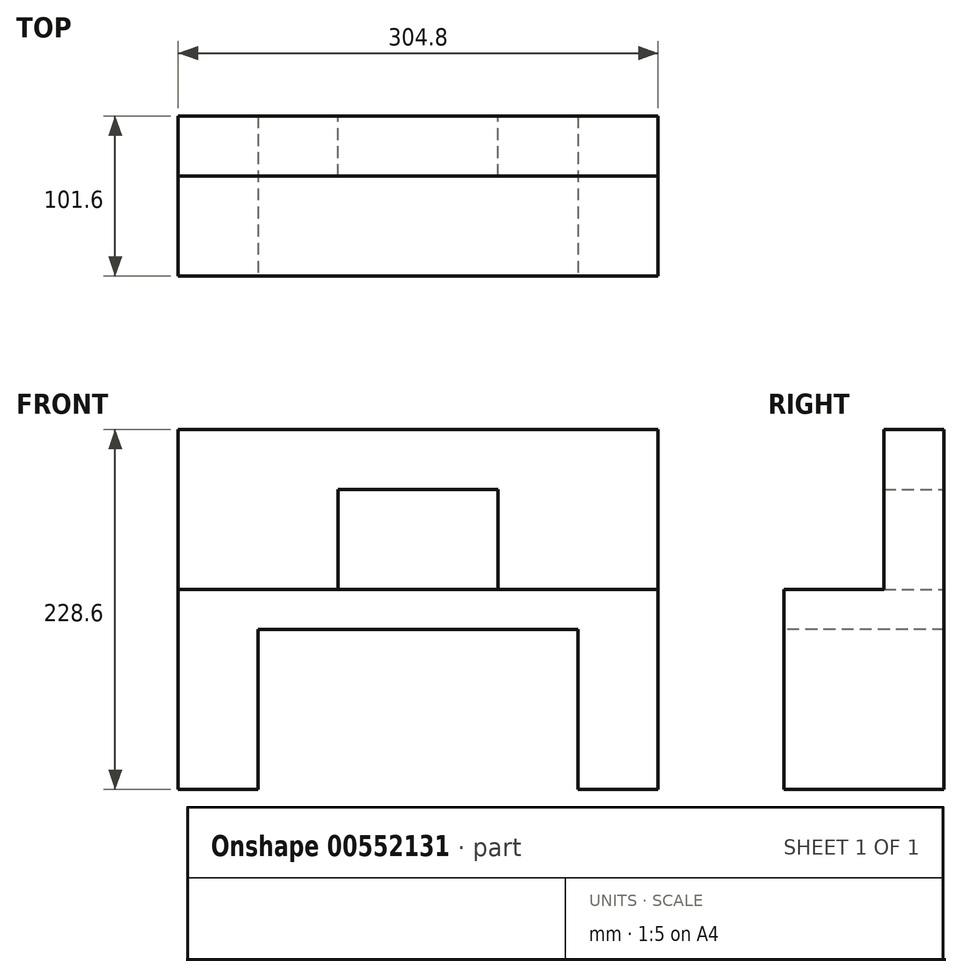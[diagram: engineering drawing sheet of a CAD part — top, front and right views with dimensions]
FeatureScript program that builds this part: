
annotation { "Feature Type Name" : "Feature", "Feature Type Description" : "" }
export const myFeature = defineFeature(function(context is Context, id is Id, definition is map)
    precondition{}
    {
        {
            var Q0;
            Q0=qCreatedBy(makeId("Top.planeOp"),FACE);
            var sketch = newSketch(context, id + "F0", { "sketchPlane" : qUnion([Q0])});
            skLineSegment(sketch, "E0.bottom", {"start": v(-249.47, 52.33) * mm, "end": v(55.33, 52.33) * mm});
            skLineSegment(sketch, "E0.top", {"start": v(-249.47, -49.27) * mm, "end": v(55.33, -49.27) * mm});
            skLineSegment(sketch, "E0.left", {"start": v(-249.47, 52.33) * mm, "end": v(-249.47, -49.27) * mm});
            skLineSegment(sketch, "E0.right", {"start": v(55.33, 52.33) * mm, "end": v(55.33, -49.27) * mm});
            skSolve(sketch);
        }
        {
            var Q0;
            Q0=makeQuery(id+"F0.imprint","IMPRINT",FACE,{"disambiguationData":[TD([[makeQuery(id+"F0.imprint","IMPRINT",EDGE,{"derivedFrom":sQuery(id+"F0.wireOp",EDGE,"E0.bottom")}),-1.0]])]});
            extrude(context, id + "F1", {"entities" : qUnion([Q0]), "depth" : 127 * mm, "offsetDistance" : 25.4 * mm});
        }
        {
            var Q0;
            Q0=makeQuery(id+"F1.opExtrude","SWEPT_FACE",FACE,{"disambiguationData":[OSD([sQuery(id+"F0.wireOp",EDGE,"E0.top")])]});
            var sketch = newSketch(context, id + "F2", { "sketchPlane" : qUnion([Q0])});
            skLineSegment(sketch, "E1", {"start": v(-198.67, 0) * mm, "end": v(-198.67, 127) * mm});
            skLineSegment(sketch, "E2", {"start": v(4.53, 0) * mm, "end": v(4.53, 127) * mm});
            skLineSegment(sketch, "E3", {"start": v(-198.67, 101.6) * mm, "end": v(4.53, 101.6) * mm});
            skLineSegment(sketch, "E4.bottom", {"start": v(-249.47, 127) * mm, "end": v(-198.67, 127) * mm});
            skLineSegment(sketch, "E4.top", {"start": v(-249.47, 63.5) * mm, "end": v(-198.67, 63.5) * mm});
            skLineSegment(sketch, "E4.left", {"start": v(-249.47, 127) * mm, "end": v(-249.47, 63.5) * mm});
            skLineSegment(sketch, "E4.right", {"start": v(-198.67, 127) * mm, "end": v(-198.67, 63.5) * mm});
            skLineSegment(sketch, "E5.bottom", {"start": v(4.53, 127) * mm, "end": v(55.33, 127) * mm});
            skLineSegment(sketch, "E5.top", {"start": v(4.53, 63.5) * mm, "end": v(55.33, 63.5) * mm});
            skLineSegment(sketch, "E5.left", {"start": v(4.53, 127) * mm, "end": v(4.53, 63.5) * mm});
            skLineSegment(sketch, "E5.right", {"start": v(55.33, 127) * mm, "end": v(55.33, 63.5) * mm});
            skLineSegment(sketch, "E6.top", {"start": v(-249.47, 0) * mm, "end": v(-198.67, 0) * mm});
            skLineSegment(sketch, "E6.left", {"start": v(-249.47, 63.5) * mm, "end": v(-249.47, 0) * mm});
            skLineSegment(sketch, "E6.right", {"start": v(-198.67, 63.5) * mm, "end": v(-198.67, 0) * mm});
            skLineSegment(sketch, "E7.top", {"start": v(4.53, 0) * mm, "end": v(55.33, 0) * mm});
            skLineSegment(sketch, "E7.left", {"start": v(4.53, 63.5) * mm, "end": v(4.53, 0) * mm});
            skLineSegment(sketch, "E7.right", {"start": v(55.33, 63.5) * mm, "end": v(55.33, 0) * mm});
            skLineSegment(sketch, "E8.bottom", {"start": v(-198.67, 127) * mm, "end": v(4.53, 127) * mm});
            skLineSegment(sketch, "E8.left", {"start": v(-198.67, 127) * mm, "end": v(-198.67, 101.6) * mm});
            skLineSegment(sketch, "E8.right", {"start": v(4.53, 127) * mm, "end": v(4.53, 101.6) * mm});
            skLineSegment(sketch, "E9.top", {"start": v(-198.67, 0) * mm, "end": v(4.53, 0) * mm});
            skLineSegment(sketch, "E9.left", {"start": v(-198.67, 101.6) * mm, "end": v(-198.67, 0) * mm});
            skLineSegment(sketch, "E9.right", {"start": v(4.53, 101.6) * mm, "end": v(4.53, 0) * mm});
            skSolve(sketch);
        }
        {
            var Q0;
            {var subQ3=sQuery(id+"F2.wireOp",EDGE,"E3");Q0=makeQuery(id+"F2.imprint","IMPRINT",FACE,{"disambiguationData":[TD([[makeQuery(id+"F2.imprint","IMPRINT",EDGE,{"derivedFrom":subQ3}),-1.0]])]});}
            extrude(context, id + "F3", {"entities" : qUnion([Q0]), "operationType" : NewBodyOperationType.REMOVE, "endBound" : BoundingType.THROUGH_ALL, "oppositeDirection" : true, "depth" : 25.4 * mm, "offsetDistance" : 25.4 * mm});
        }
        {
            var Q0;
            Q0=makeQuery(id+"F1.opExtrude","CAP_FACE",FACE,{"disambiguationData":[OSD([sQuery(id+"F0.wireOp",EDGE,"E0.bottom"),sQuery(id+"F0.wireOp",EDGE,"E0.top"),sQuery(id+"F0.wireOp",EDGE,"E0.left"),sQuery(id+"F0.wireOp",EDGE,"E0.right")])],"isStart":false});
            var sketch = newSketch(context, id + "F4", { "sketchPlane" : qUnion([Q0])});
            skLineSegment(sketch, "E10", {"start": v(-249.47, 14.23) * mm, "end": v(55.33, 14.23) * mm});
            skLineSegment(sketch, "E11", {"start": v(-198.67, 14.23) * mm, "end": v(-198.67, 52.33) * mm});
            skLineSegment(sketch, "E12", {"start": v(4.53, 14.23) * mm, "end": v(4.53, 52.33) * mm});
            skLineSegment(sketch, "E13", {"start": v(-147.87, 14.23) * mm, "end": v(-147.87, 52.33) * mm});
            skLineSegment(sketch, "E14", {"start": v(-46.27, 14.23) * mm, "end": v(-46.27, 52.33) * mm});
            skSolve(sketch);
        }
        {
            var Q0;
            {var subQ3=sQuery(id+"F4.wireOp",EDGE,"E11");Q0=makeQuery(id+"F4.imprint","IMPRINT",FACE,{"disambiguationData":[TD([[makeQuery(id+"F4.imprint","IMPRINT",EDGE,{"derivedFrom":subQ3}),1.0]])]});}
            var Q1;
            {var subQ0=sQuery(id+"F4.wireOp",EDGE,"E11");Q1=makeQuery(id+"F4.imprint","IMPRINT",FACE,{"disambiguationData":[TD([[makeQuery(id+"F4.imprint","IMPRINT",EDGE,{"derivedFrom":subQ0}),-1.0]])]});}
            var Q2;
            {var subQ0=sQuery(id+"F4.wireOp",EDGE,"E12");Q2=makeQuery(id+"F4.imprint","IMPRINT",FACE,{"disambiguationData":[TD([[makeQuery(id+"F4.imprint","IMPRINT",EDGE,{"derivedFrom":subQ0}),1.0]])]});}
            var Q3;
            {var subQ3=sQuery(id+"F4.wireOp",EDGE,"E12");Q3=makeQuery(id+"F4.imprint","IMPRINT",FACE,{"disambiguationData":[TD([[makeQuery(id+"F4.imprint","IMPRINT",EDGE,{"derivedFrom":subQ3}),-1.0]])]});}
            extrude(context, id + "F5", {"entities" : qUnion([Q0, Q1, Q2, Q3]), "operationType" : NewBodyOperationType.ADD, "depth" : 101.6 * mm, "offsetDistance" : 25.4 * mm});
        }
        {
            var Q0;
            Q0=makeQuery(id+"F5.opExtrude","SWEPT_FACE",FACE,{"disambiguationData":[OSD([sQuery(id+"F4.wireOp",EDGE,"E13")])]});
            var sketch = newSketch(context, id + "F6", { "sketchPlane" : qUnion([Q0])});
            skLineSegment(sketch, "E15", {"start": v(14.23, 190.5) * mm, "end": v(52.33, 190.5) * mm});
            skSolve(sketch);
        }
        {
            var Q0;
            {var subQ0=sQuery(id+"F6.wireOp",EDGE,"E15");Q0=makeQuery(id+"F6.imprint","IMPRINT",FACE,{"disambiguationData":[TD([[makeQuery(id+"F6.imprint","IMPRINT",EDGE,{"derivedFrom":subQ0}),1.0]])]});}
            extrude(context, id + "F7", {"entities" : qUnion([Q0]), "operationType" : NewBodyOperationType.ADD, "depth" : 101.6 * mm, "offsetDistance" : 25.4 * mm});
        }
    });
